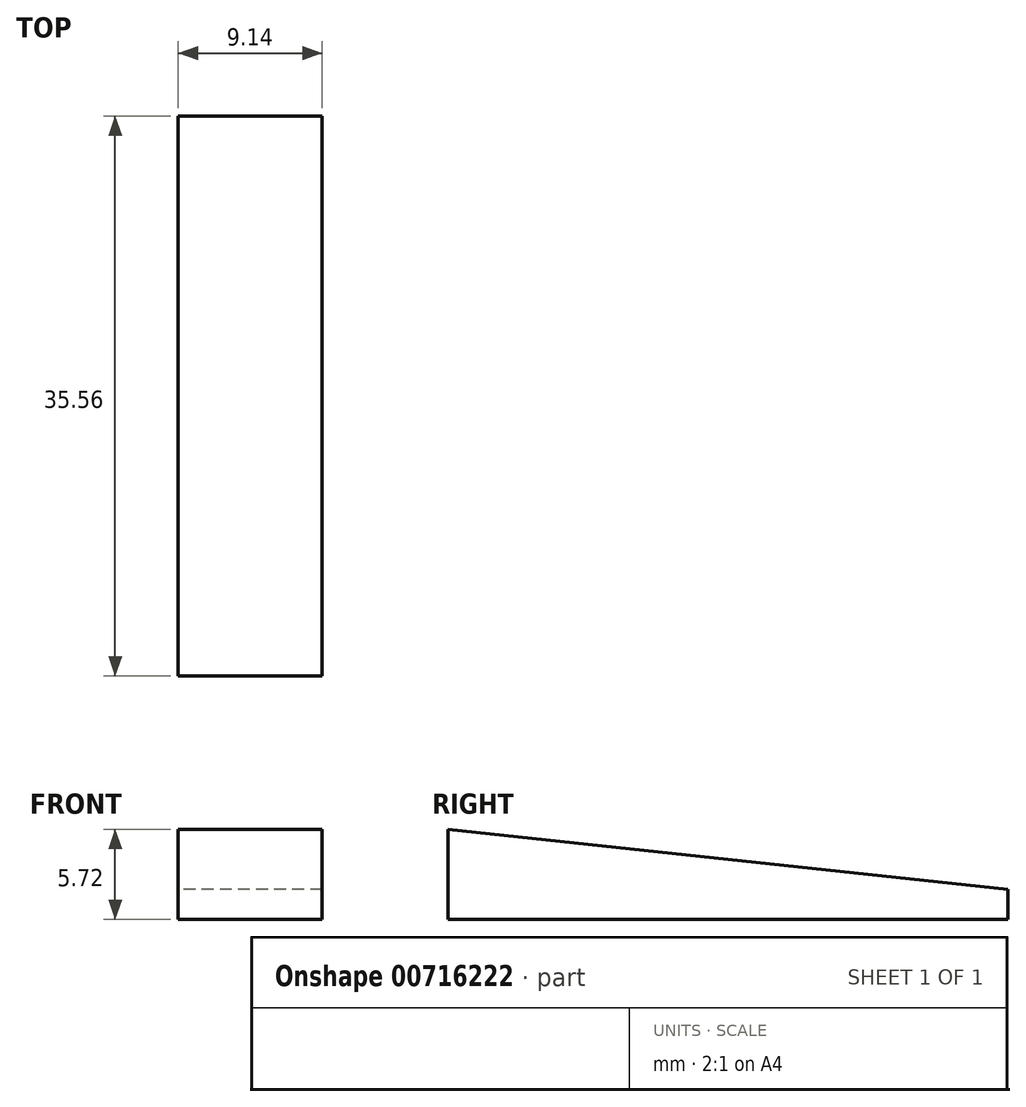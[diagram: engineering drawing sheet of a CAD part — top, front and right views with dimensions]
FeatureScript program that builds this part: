
annotation { "Feature Type Name" : "Feature", "Feature Type Description" : "" }
export const myFeature = defineFeature(function(context is Context, id is Id, definition is map)
    precondition{}
    {
        {
            var Q0;
            Q0=qCreatedBy(makeId("Right.planeOp"),FACE);
            var sketch = newSketch(context, id + "F0", { "sketchPlane" : qUnion([Q0])});
            skLineSegment(sketch, "E0", {"start": v(0, 0) * mm, "end": v(-35.56, 0) * mm});
            skLineSegment(sketch, "E1", {"start": v(-35.56, 0) * mm, "end": v(-35.56, 3.8) * mm});
            skLineSegment(sketch, "E2", {"start": v(-35.56, 3.8) * mm, "end": v(0, 0) * mm});
            skSolve(sketch);
        }
        {
            var Q0;
            Q0=makeQuery(id+"F0.imprint","IMPRINT",FACE,{"disambiguationData":[TD([[makeQuery(id+"F0.imprint","IMPRINT",EDGE,{"derivedFrom":sQuery(id+"F0.wireOp",EDGE,"E0")}),-1.0]])]});
            extrude(context, id + "F1", {"entities" : qUnion([Q0]), "depth" : 9.14 * mm, "offsetDistance" : 25.4 * mm});
        }
        {
            var Q0;
            Q0=makeQuery(id+"F1.opExtrude","SWEPT_FACE",FACE,{"disambiguationData":[OSD([sQuery(id+"F0.wireOp",EDGE,"E0")])]});
            extrude(context, id + "F2", {"entities" : qUnion([Q0]), "operationType" : NewBodyOperationType.ADD, "depth" : 1.9 * mm, "offsetDistance" : 25.4 * mm});
        }
    });
